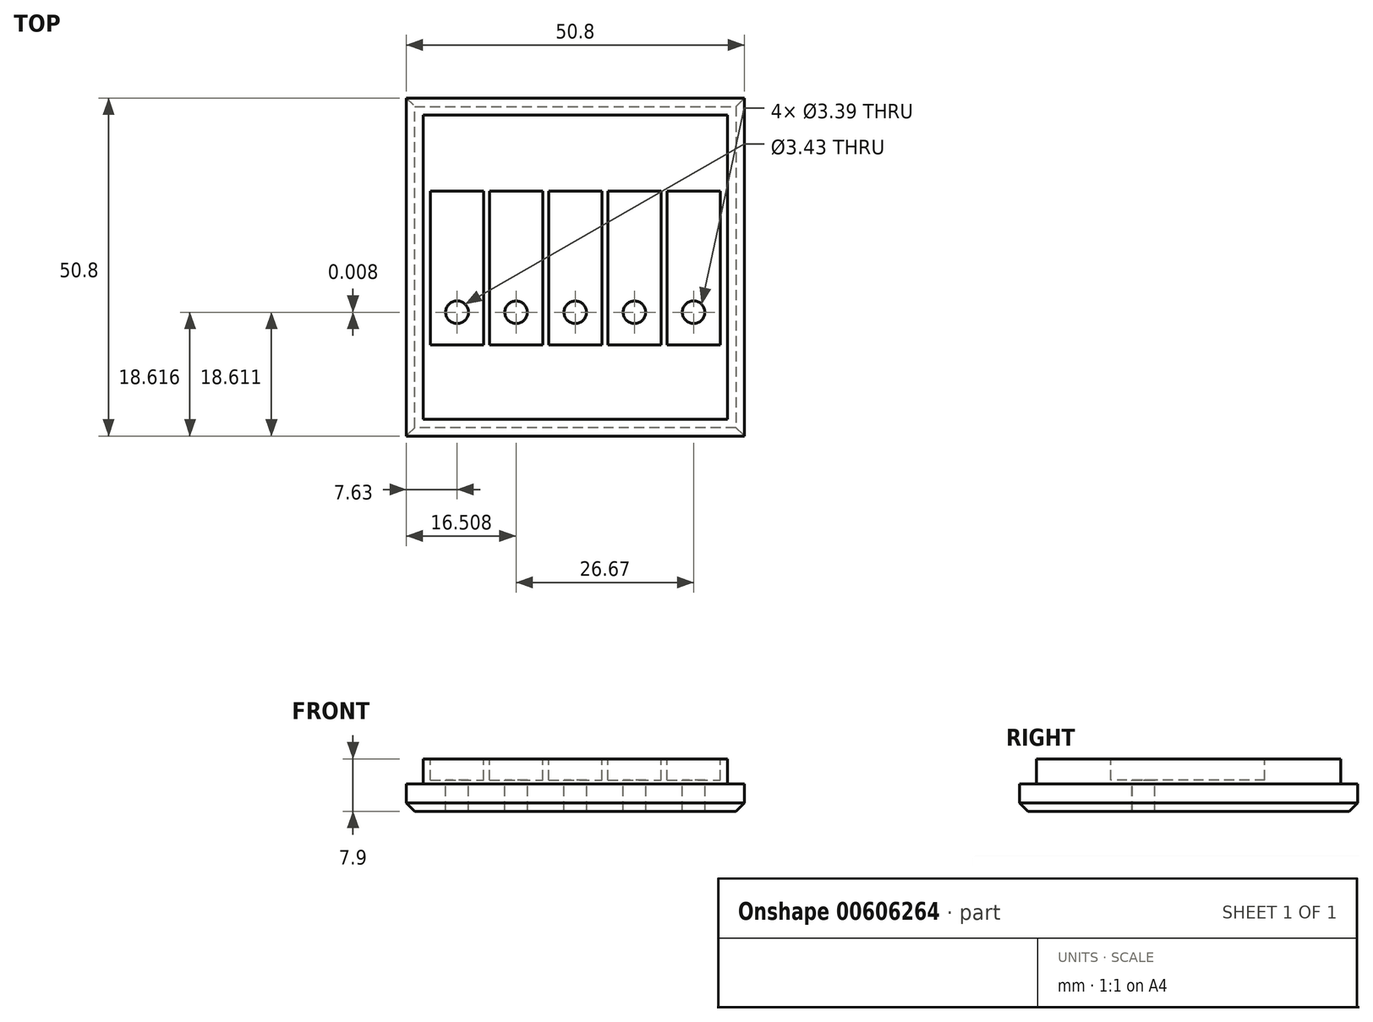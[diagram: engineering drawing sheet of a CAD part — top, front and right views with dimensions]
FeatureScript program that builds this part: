
annotation { "Feature Type Name" : "Feature", "Feature Type Description" : "" }
export const myFeature = defineFeature(function(context is Context, id is Id, definition is map)
    precondition{}
    {
        {
            var Q0;
            Q0=qCreatedBy(makeId("Top.planeOp"),FACE);
            var sketch = newSketch(context, id + "F0", { "sketchPlane" : qUnion([Q0])});
            skLineSegment(sketch, "E0.bottom", {"start": v(-12.32, 40.12) * mm, "end": v(38.48, 40.12) * mm});
            skLineSegment(sketch, "E0.top", {"start": v(-12.32, -10.68) * mm, "end": v(38.48, -10.68) * mm});
            skLineSegment(sketch, "E0.left", {"start": v(-12.32, 40.12) * mm, "end": v(-12.32, -10.68) * mm});
            skLineSegment(sketch, "E0.right", {"start": v(38.48, 40.12) * mm, "end": v(38.48, -10.68) * mm});
            skSolve(sketch);
        }
        {
            var Q0;
            Q0=makeQuery(id+"F0.imprint","IMPRINT",FACE,{"disambiguationData":[TD([[makeQuery(id+"F0.imprint","IMPRINT",EDGE,{"derivedFrom":sQuery(id+"F0.wireOp",EDGE,"E0.bottom")}),-1.0]])]});
            extrude(context, id + "F1", {"entities" : qUnion([Q0]), "depth" : 4.13 * mm, "offsetDistance" : 25.4 * mm});
        }
        {
            var Q0;
            Q0=makeQuery(id+"F1.opExtrude","CAP_FACE",FACE,{"disambiguationData":[OSD([sQuery(id+"F0.wireOp",EDGE,"E0.bottom"),sQuery(id+"F0.wireOp",EDGE,"E0.top"),sQuery(id+"F0.wireOp",EDGE,"E0.left"),sQuery(id+"F0.wireOp",EDGE,"E0.right")])],"isStart":true});
            var sketch = newSketch(context, id + "F2", { "sketchPlane" : qUnion([Q0])});
            skLineSegment(sketch, "E1.bottom", {"start": v(-10.03, 8.4) * mm, "end": v(36.2, 8.4) * mm});
            skLineSegment(sketch, "E1.top", {"start": v(-10.03, -37.84) * mm, "end": v(36.2, -37.84) * mm});
            skLineSegment(sketch, "E1.left", {"start": v(-10.03, 8.4) * mm, "end": v(-10.03, -37.84) * mm});
            skLineSegment(sketch, "E1.right", {"start": v(36.2, 8.4) * mm, "end": v(36.2, -37.84) * mm});
            skSolve(sketch);
        }
        {
            var Q0;
            Q0=makeQuery(id+"F1.opExtrude","CAP_FACE",FACE,{"disambiguationData":[OSD([sQuery(id+"F0.wireOp",EDGE,"E0.bottom"),sQuery(id+"F0.wireOp",EDGE,"E0.top"),sQuery(id+"F0.wireOp",EDGE,"E0.left"),sQuery(id+"F0.wireOp",EDGE,"E0.right")])],"isStart":false});
            var sketch = newSketch(context, id + "F3", { "sketchPlane" : qUnion([Q0])});
            skLineSegment(sketch, "E2.bottom", {"start": v(-9.78, 37.58) * mm, "end": v(35.94, 37.58) * mm});
            skLineSegment(sketch, "E2.top", {"start": v(-9.78, -8.14) * mm, "end": v(35.94, -8.14) * mm});
            skLineSegment(sketch, "E2.left", {"start": v(-9.78, 37.58) * mm, "end": v(-9.78, -8.14) * mm});
            skLineSegment(sketch, "E2.right", {"start": v(35.94, 37.58) * mm, "end": v(35.94, -8.14) * mm});
            skSolve(sketch);
        }
        {
            var Q0;
            Q0=makeQuery(id+"F3.imprint","IMPRINT",FACE,{"disambiguationData":[TD([[makeQuery(id+"F3.imprint","IMPRINT",EDGE,{"derivedFrom":sQuery(id+"F3.wireOp",EDGE,"E2.bottom")}),-1.0]])]});
            extrude(context, id + "F4", {"entities" : qUnion([Q0]), "operationType" : NewBodyOperationType.ADD, "depth" : 3.77 * mm, "offsetDistance" : 25.4 * mm});
        }
        {
            var Q0;
            Q0=makeQuery(id+"F4.opExtrude","CAP_FACE",FACE,{"disambiguationData":[OSD([sQuery(id+"F3.wireOp",EDGE,"E2.bottom"),sQuery(id+"F3.wireOp",EDGE,"E2.top"),sQuery(id+"F3.wireOp",EDGE,"E2.left"),sQuery(id+"F3.wireOp",EDGE,"E2.right")])],"isStart":false});
            var sketch = newSketch(context, id + "F5", { "sketchPlane" : qUnion([Q0])});
            skLineSegment(sketch, "E3.bottom", {"start": v(-8.69, 26.15) * mm, "end": v(-0.69, 26.15) * mm});
            skLineSegment(sketch, "E3.top", {"start": v(-8.69, 3.04) * mm, "end": v(-0.69, 3.04) * mm});
            skLineSegment(sketch, "E3.left", {"start": v(-8.69, 26.15) * mm, "end": v(-8.69, 3.04) * mm});
            skLineSegment(sketch, "E3.right", {"start": v(-0.69, 26.15) * mm, "end": v(-0.69, 3.04) * mm});
            skLineSegment(sketch, "E4.1.0.0", {"start": v(0.2, 26.15) * mm, "end": v(0.2, 3.04) * mm});
            skLineSegment(sketch, "E4.1.0.1", {"start": v(8.2, 26.15) * mm, "end": v(8.2, 3.04) * mm});
            skLineSegment(sketch, "E4.1.0.2", {"start": v(0.2, 26.15) * mm, "end": v(8.2, 26.15) * mm});
            skLineSegment(sketch, "E4.1.0.3", {"start": v(0.2, 3.04) * mm, "end": v(8.2, 3.04) * mm});
            skLineSegment(sketch, "E4.2.0.0", {"start": v(9.1, 26.15) * mm, "end": v(9.1, 3.04) * mm});
            skLineSegment(sketch, "E4.2.0.1", {"start": v(17.1, 26.15) * mm, "end": v(17.1, 3.04) * mm});
            skLineSegment(sketch, "E4.2.0.2", {"start": v(9.1, 26.15) * mm, "end": v(17.1, 26.15) * mm});
            skLineSegment(sketch, "E4.2.0.3", {"start": v(9.1, 3.04) * mm, "end": v(17.1, 3.04) * mm});
            skLineSegment(sketch, "E4.direction1", {"start": v(-8.69, 3.04) * mm, "end": v(0.2, 3.04) * mm, "construction": true});
            skLineSegment(sketch, "E5.0.3.0", {"start": v(17.98, 26.15) * mm, "end": v(17.98, 3.04) * mm});
            skLineSegment(sketch, "E5.3.3.0", {"start": v(25.98, 26.15) * mm, "end": v(25.98, 3.04) * mm});
            skLineSegment(sketch, "E5.6.3.0", {"start": v(17.98, 26.15) * mm, "end": v(25.98, 26.15) * mm});
            skLineSegment(sketch, "E5.9.3.0", {"start": v(17.98, 3.04) * mm, "end": v(25.98, 3.04) * mm});
            skLineSegment(sketch, "E5.0.4.0", {"start": v(26.87, 26.15) * mm, "end": v(26.87, 3.04) * mm});
            skLineSegment(sketch, "E5.3.4.0", {"start": v(34.87, 26.15) * mm, "end": v(34.87, 3.04) * mm});
            skLineSegment(sketch, "E5.6.4.0", {"start": v(26.87, 26.15) * mm, "end": v(34.87, 26.15) * mm});
            skLineSegment(sketch, "E5.9.4.0", {"start": v(26.87, 3.04) * mm, "end": v(34.87, 3.04) * mm});
            skSolve(sketch);
        }
        {
            var Q0;
            Q0=makeQuery(id+"F5.imprint","IMPRINT",FACE,{"disambiguationData":[TD([[makeQuery(id+"F5.imprint","IMPRINT",EDGE,{"derivedFrom":sQuery(id+"F5.wireOp",EDGE,"E4.1.0.0")}),1.0]])]});
            var Q1;
            Q1=makeQuery(id+"F5.imprint","IMPRINT",FACE,{"disambiguationData":[TD([[makeQuery(id+"F5.imprint","IMPRINT",EDGE,{"derivedFrom":sQuery(id+"F5.wireOp",EDGE,"E4.2.0.0")}),1.0]])]});
            var Q2;
            Q2=makeQuery(id+"F5.imprint","IMPRINT",FACE,{"disambiguationData":[TD([[makeQuery(id+"F5.imprint","IMPRINT",EDGE,{"derivedFrom":sQuery(id+"F5.wireOp",EDGE,"E5.0.3.0")}),1.0]])]});
            var Q3;
            Q3=makeQuery(id+"F5.imprint","IMPRINT",FACE,{"disambiguationData":[TD([[makeQuery(id+"F5.imprint","IMPRINT",EDGE,{"derivedFrom":sQuery(id+"F5.wireOp",EDGE,"E5.0.4.0")}),1.0]])]});
            var Q4;
            Q4=makeQuery(id+"F5.imprint","IMPRINT",FACE,{"disambiguationData":[TD([[makeQuery(id+"F5.imprint","IMPRINT",EDGE,{"derivedFrom":sQuery(id+"F5.wireOp",EDGE,"E3.bottom")}),-1.0]])]});
            extrude(context, id + "F6", {"entities" : qUnion([Q0, Q1, Q2, Q3, Q4]), "operationType" : NewBodyOperationType.REMOVE, "oppositeDirection" : true, "depth" : 3.2 * mm, "offsetDistance" : 25.4 * mm});
        }
        {
            var Q0;
            Q0=makeQuery(id+"F6.boolean.opBoolean","COPY",FACE,{"derivedFrom":makeQuery(id+"F6.opExtrude","CAP_FACE",FACE,{"disambiguationData":[OSD([sQuery(id+"F5.wireOp",EDGE,"E3.bottom"),sQuery(id+"F5.wireOp",EDGE,"E3.top"),sQuery(id+"F5.wireOp",EDGE,"E3.left"),sQuery(id+"F5.wireOp",EDGE,"E3.right")])],"isStart":false})});
            var sketch = newSketch(context, id + "F7", { "sketchPlane" : qUnion([Q0])});
            skCircle(sketch, "E6", {"center": v(-4.69, 7.94) * mm, "radius": 1.71 * mm});
            skLineSegment(sketch, "E7.bottom", {"start": v(3.2, -6.76) * mm, "end": v(26.27, -6.76) * mm});
            skLineSegment(sketch, "E7.top", {"start": v(3.2, 1.24) * mm, "end": v(26.27, 1.24) * mm});
            skLineSegment(sketch, "E7.left", {"start": v(3.2, -6.76) * mm, "end": v(3.2, 1.24) * mm});
            skLineSegment(sketch, "E7.right", {"start": v(26.27, -6.76) * mm, "end": v(26.27, 1.24) * mm});
            skLineSegment(sketch, "E8.bottom", {"start": v(3.1, 3.08) * mm, "end": v(26.16, 3.08) * mm});
            skLineSegment(sketch, "E8.top", {"start": v(3.1, 11.08) * mm, "end": v(26.16, 11.08) * mm});
            skLineSegment(sketch, "E8.left", {"start": v(3.1, 3.08) * mm, "end": v(3.1, 11.08) * mm});
            skLineSegment(sketch, "E8.right", {"start": v(26.16, 3.08) * mm, "end": v(26.16, 11.08) * mm});
            skCircle(sketch, "E9", {"center": v(21.41, -2.74) * mm, "radius": 1.71 * mm});
            skCircle(sketch, "E10", {"center": v(21.31, 7.1) * mm, "radius": 1.71 * mm});
            skSolve(sketch);
        }
        {
            var Q0;
            Q0=makeQuery(id+"F7.imprint","IMPRINT",FACE,{"disambiguationData":[TD([[makeQuery(id+"F7.imprint","IMPRINT",EDGE,{"derivedFrom":sQuery(id+"F7.wireOp",EDGE,"E6")}),1.0]])]});
            var Q1;
            Q1 = qSketchRegion(id + "F10", true);
            extrude(context, id + "F8", {"entities" : qUnion([Q0, Q1]), "operationType" : NewBodyOperationType.REMOVE, "oppositeDirection" : true, "depth" : 25.4 * mm, "offsetDistance" : 25.4 * mm});
        }
        {
            var Q0;
            Q0=makeQuery(id+"F1.opExtrude","CAP_EDGE",EDGE,{"disambiguationData":[OSD([sQuery(id+"F0.wireOp",EDGE,"E0.top")])],"isStart":true});
            var Q1;
            Q1=makeQuery(id+"F1.opExtrude","CAP_EDGE",EDGE,{"disambiguationData":[OSD([sQuery(id+"F0.wireOp",EDGE,"E0.bottom")])],"isStart":true});
            var Q2;
            Q2=makeQuery(id+"F1.opExtrude","CAP_EDGE",EDGE,{"disambiguationData":[OSD([sQuery(id+"F0.wireOp",EDGE,"E0.left")])],"isStart":true});
            var Q3;
            Q3=makeQuery(id+"F1.opExtrude","CAP_EDGE",EDGE,{"disambiguationData":[OSD([sQuery(id+"F0.wireOp",EDGE,"E0.right")])],"isStart":true});
            chamfer(context, id + "F9", {"entities" : qUnion([Q0, Q1, Q2, Q3]), "width" : 1.27 * mm, "tangentPropagation" : true});
        }
        {
            var Q0;
            Q0=makeQuery(id+"F6.boolean.opBoolean","COPY",FACE,{"derivedFrom":makeQuery(id+"F6.opExtrude","CAP_FACE",FACE,{"disambiguationData":[OSD([sQuery(id+"F5.wireOp",EDGE,"E4.1.0.0"),sQuery(id+"F5.wireOp",EDGE,"E4.1.0.1"),sQuery(id+"F5.wireOp",EDGE,"E4.1.0.2"),sQuery(id+"F5.wireOp",EDGE,"E4.1.0.3")])],"isStart":false})});
            var sketch = newSketch(context, id + "F10", { "sketchPlane" : qUnion([Q0])});
            skCircle(sketch, "E11", {"center": v(4.19, 7.93) * mm, "radius": 1.7 * mm});
            skCircle(sketch, "E12", {"center": v(13.08, 7.93) * mm, "radius": 1.7 * mm});
            skCircle(sketch, "E13", {"center": v(21.97, 7.93) * mm, "radius": 1.7 * mm});
            skCircle(sketch, "E14", {"center": v(30.86, 7.94) * mm, "radius": 1.7 * mm});
            skSolve(sketch);
        }
        {
            var Q0;
            Q0=makeQuery(id+"F10.imprint","IMPRINT",FACE,{"disambiguationData":[TD([[makeQuery(id+"F10.imprint","IMPRINT",EDGE,{"derivedFrom":sQuery(id+"F10.wireOp",EDGE,"E11")}),1.0]])]});
            var Q1;
            Q1=makeQuery(id+"F10.imprint","IMPRINT",FACE,{"disambiguationData":[TD([[makeQuery(id+"F10.imprint","IMPRINT",EDGE,{"derivedFrom":sQuery(id+"F10.wireOp",EDGE,"E12")}),1.0]])]});
            var Q2;
            Q2=makeQuery(id+"F10.imprint","IMPRINT",FACE,{"disambiguationData":[TD([[makeQuery(id+"F10.imprint","IMPRINT",EDGE,{"derivedFrom":sQuery(id+"F10.wireOp",EDGE,"E13")}),1.0]])]});
            var Q3;
            Q3=makeQuery(id+"F10.imprint","IMPRINT",FACE,{"disambiguationData":[TD([[makeQuery(id+"F10.imprint","IMPRINT",EDGE,{"derivedFrom":sQuery(id+"F10.wireOp",EDGE,"E14")}),1.0]])]});
            extrude(context, id + "F11", {"entities" : qUnion([Q0, Q1, Q2, Q3]), "operationType" : NewBodyOperationType.REMOVE, "oppositeDirection" : true, "depth" : 25.4 * mm, "offsetDistance" : 25.4 * mm});
        }
    });
